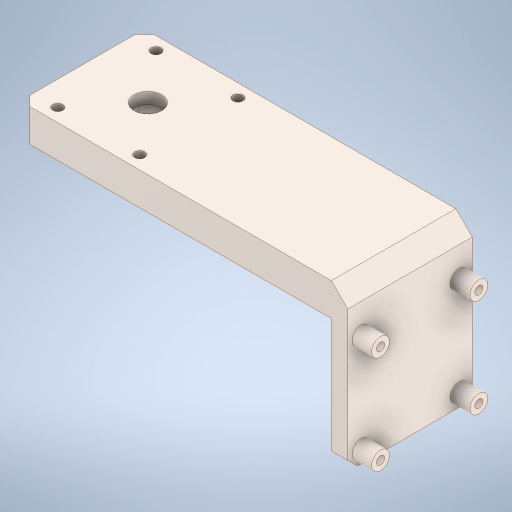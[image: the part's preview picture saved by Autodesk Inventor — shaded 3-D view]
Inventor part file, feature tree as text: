
AUTODESK INVENTOR PART (.ipt)
format: ipt  version: 2023 (Build 270158000, 158)  size: 450,048 bytes
history: mixed  units: mm
features: extrude x9, sketch x8, chamfer x3, fillet x1, plane x1, other x1, imported_body x1
ambient origin geometry x8: Origin, YZ Plane, XZ Plane, XY Plane, X Axis, Y Axis, Z Axis, Center Point
bodies: Solid1 (imported_parasolid)
feature tree (24):
  extrude  "Extrusion1"  Depth=38.0mm
  extrude  "Extrusion2"  Depth=5.0mm TaperAngle=0.0deg
  extrude  "Extrusion3"  Depth=2.5mm
  extrude  "Extrusion4"  Depth=2.5mm
  fillet  "Fillet1"  Radius=4.0mm
  extrude  "Extrusion6"  Depth=5.0mm TaperAngle=0.0deg
  extrude  "Extrusion7"  Depth=5.5mm
  extrude  "Extrusion8"  Depth=5.5mm
  extrude  "Extrusion9"  Depth=5.0mm
  chamfer  "Chamfer1"  Distance=70.0mm
  chamfer  "Chamfer2"  Distance=10.0mm
  chamfer  "Chamfer3"  Distance=100.0mm
  plane  "Work Plane1"
  extrude  "Extrusion10"  Depth=6.5mm
  sketch  "Sketch1"  dims[d0=5.0mm d1=0.0mm d2=38.0mm]
  sketch  "Sketch3"  dims[d3=38.0mm d4=5.0mm d5=0.0mm]
  sketch  "Sketch4"  dims[d6=2.5mm d7=2.5mm]
  sketch  "Sketch7"  dims[d8=2.5mm d9=2.5mm d10=4.0mm]
  sketch  "Sketch9"  dims[d11=4.0mm d12=5.0mm d13=0.0mm]
  sketch  "Sketch10"  dims[d14=5.5mm d15=5.5mm]
  sketch  "Sketch11"  dims[d16=5.5mm d17=5.5mm]
  sketch  "Sketch12"  dims[d18=6.0mm d19=0.0mm d20=5.0mm d23=70.0mm d24=0.0mm d25=10.0mm d26=100.0mm d27=0.0mm d28=25.0mm d29=30.0mm d30=8.5mm d31=3.1mm d32=3.1mm d33=3.1mm d34=3.1mm d35=20.0mm d36=100.0mm d37=0.0mm d38=13.2mm d39=6.5mm d40=0.0mm d41=3.0mm d42=2.0mm d43=45.0deg d44=3.0mm d45=2.0mm d46=45.0deg d47=5.0mm d48=2.0mm d49=45.0deg d50=45.0deg d51=6.5mm d52=0.0mm]
  other  "Boss-Extrude6"
  imported_body  NMx_Import_Brep_tag  [imported B-rep: ~40 faces, bbox_mm=[106.0, 48.0, 38.0]]
